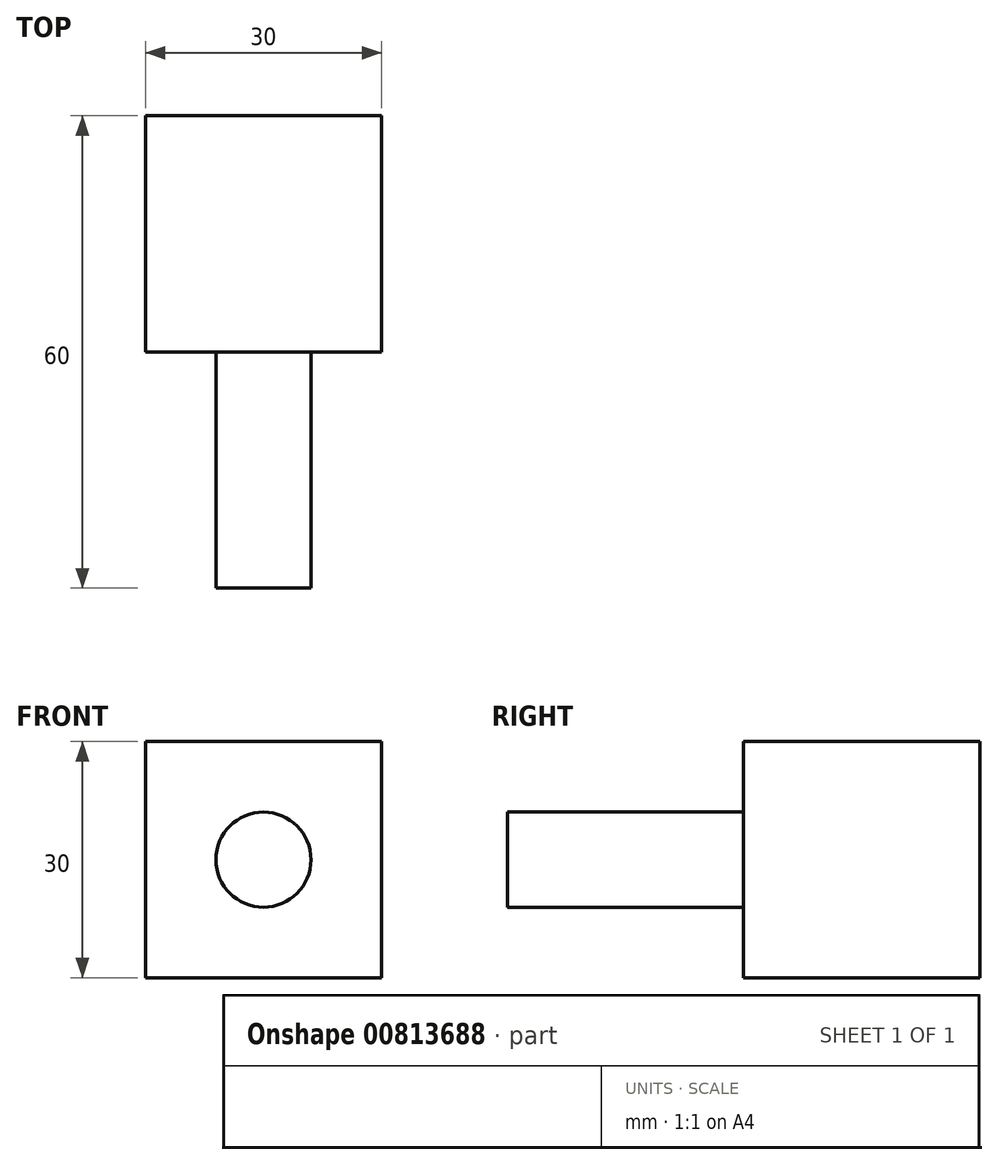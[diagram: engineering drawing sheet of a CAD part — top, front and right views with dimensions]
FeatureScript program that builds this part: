
annotation { "Feature Type Name" : "Feature", "Feature Type Description" : "" }
export const myFeature = defineFeature(function(context is Context, id is Id, definition is map)
    precondition{}
    {
        {
            var Q0;
            Q0=qCreatedBy(makeId("Front.planeOp"),FACE);
            var sketch = newSketch(context, id + "F0", { "sketchPlane" : qUnion([Q0])});
            skLineSegment(sketch, "E0.bottom", {"start": v(15, -15) * mm, "end": v(-15, -15) * mm});
            skLineSegment(sketch, "E0.top", {"start": v(15, 15) * mm, "end": v(-15, 15) * mm});
            skLineSegment(sketch, "E0.left", {"start": v(15, -15) * mm, "end": v(15, 15) * mm});
            skLineSegment(sketch, "E0.right", {"start": v(-15, -15) * mm, "end": v(-15, 15) * mm});
            skPoint(sketch, "E0.middle", {"position": v(0, 0) * mm});
            skSolve(sketch);
        }
        {
            var Q0;
            Q0=makeQuery(id+"F0.imprint","IMPRINT",FACE,{"disambiguationData":[TD([[makeQuery(id+"F0.imprint","IMPRINT",EDGE,{"derivedFrom":sQuery(id+"F0.wireOp",EDGE,"E0.bottom")}),-1.0]])]});
            extrude(context, id + "F1", {"entities" : qUnion([Q0]), "endBound" : BoundingType.SYMMETRIC, "depth" : 30 * mm, "offsetDistance" : 25 * mm});
        }
        {
            var Q0;
            Q0=makeQuery(id+"F1.opExtrude","CAP_FACE",FACE,{"disambiguationData":[OSD([sQuery(id+"F0.wireOp",EDGE,"E0.bottom"),sQuery(id+"F0.wireOp",EDGE,"E0.top"),sQuery(id+"F0.wireOp",EDGE,"E0.left"),sQuery(id+"F0.wireOp",EDGE,"E0.right")])],"isStart":false});
            var sketch = newSketch(context, id + "F2", { "sketchPlane" : qUnion([Q0])});
            skCircle(sketch, "E1", {"center": v(0, 0) * mm, "radius": 6.04 * mm});
            skSolve(sketch);
        }
        {
            var Q0;
            Q0 = qSketchRegion(id + "F2", true);
            extrude(context, id + "F3", {"entities" : qUnion([Q0]), "operationType" : NewBodyOperationType.ADD, "depth" : 30 * mm, "offsetDistance" : 25 * mm});
        }
    });
